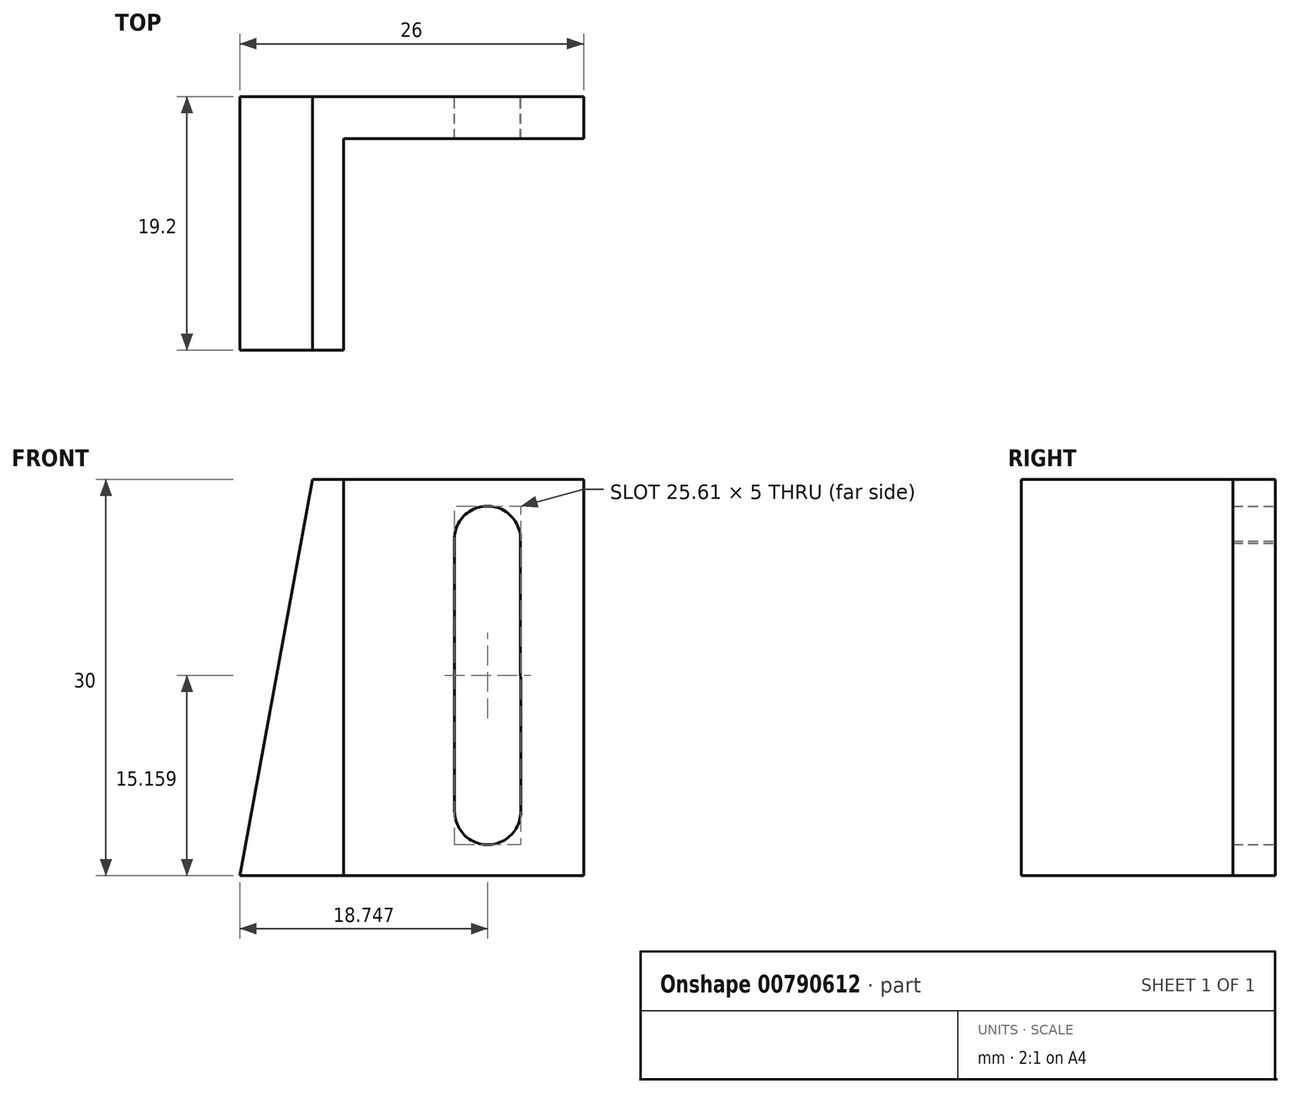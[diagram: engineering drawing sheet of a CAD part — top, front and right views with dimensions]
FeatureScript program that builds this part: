
annotation { "Feature Type Name" : "Feature", "Feature Type Description" : "" }
export const myFeature = defineFeature(function(context is Context, id is Id, definition is map)
    precondition{}
    {
        {
            var Q0;
            Q0=qCreatedBy(makeId("Front.planeOp"),FACE);
            var sketch = newSketch(context, id + "F0", { "sketchPlane" : qUnion([Q0])});
            skLineSegment(sketch, "E0", {"start": v(0, 30) * mm, "end": v(0, 0) * mm});
            skLineSegment(sketch, "E1", {"start": v(-18, 0) * mm, "end": v(-26, 0) * mm});
            skLineSegment(sketch, "E2", {"start": v(-26, 0) * mm, "end": v(-20.5, 30) * mm});
            skLineSegment(sketch, "E3", {"start": v(-20.5, 30) * mm, "end": v(0, 30) * mm});
            skLineSegment(sketch, "E4", {"start": v(-18, 0) * mm, "end": v(0, 0) * mm});
            skLineSegment(sketch, "E5", {"start": v(-18, 0) * mm, "end": v(-18, 30) * mm});
            skArc(sketch, "E6", {"start": v(-4.78, 25.31) * mm, "mid": v(-7.35, 27.96) * mm, "end": v(-9.75, 25.16) * mm});
            skArc(sketch, "E7", {"start": v(-9.75, 4.86) * mm, "mid": v(-7.25, 2.36) * mm, "end": v(-4.75, 4.86) * mm});
            skLineSegment(sketch, "E8", {"start": v(-9.75, 25.16) * mm, "end": v(-9.75, 4.86) * mm});
            skLineSegment(sketch, "E9", {"start": v(-4.78, 25.31) * mm, "end": v(-4.75, 4.86) * mm});
            skSolve(sketch);
        }
        {
            var Q0;
            {var subQ2=sQuery(id+"F0.wireOp",EDGE,"E0");Q0=makeQuery(id+"F0.imprint","IMPRINT",FACE,{"disambiguationData":[TD([[makeQuery(id+"F0.imprint","IMPRINT",EDGE,{"derivedFrom":subQ2}),-1.0]])]});}
            var Q1;
            Q1=makeQuery(id+"F0.imprint","IMPRINT",FACE,{"disambiguationData":[TD([[makeQuery(id+"F0.imprint","IMPRINT",EDGE,{"derivedFrom":sQuery(id+"F0.wireOp",EDGE,"E1")}),-1.0]])]});
            extrude(context, id + "F1", {"entities" : qUnion([Q0, Q1]), "depth" : 3.2 * mm, "offsetDistance" : 25 * mm});
        }
        {
            var Q0;
            Q0=makeQuery(id+"F1.opExtrude","CAP_FACE",FACE,{"disambiguationData":[OSD([sQuery(id+"F0.wireOp",EDGE,"E0"),sQuery(id+"F0.wireOp",EDGE,"E1"),sQuery(id+"F0.wireOp",EDGE,"E2"),sQuery(id+"F0.wireOp",EDGE,"E3"),sQuery(id+"F0.wireOp",EDGE,"E4"),sQuery(id+"F0.wireOp",EDGE,"E6"),sQuery(id+"F0.wireOp",EDGE,"E7"),sQuery(id+"F0.wireOp",EDGE,"E8"),sQuery(id+"F0.wireOp",EDGE,"E9")])],"isStart":false});
            var sketch = newSketch(context, id + "F2", { "sketchPlane" : qUnion([Q0])});
            skLineSegment(sketch, "E10", {"start": v(-18.14, 30) * mm, "end": v(-18.14, 0) * mm});
            skLineSegment(sketch, "E11", {"start": v(-18.14, 30) * mm, "end": v(-20.5, 30) * mm});
            skLineSegment(sketch, "E12", {"start": v(-20.5, 30) * mm, "end": v(-26, 0) * mm});
            skLineSegment(sketch, "E13", {"start": v(-26, 0) * mm, "end": v(-18.14, 0) * mm});
            skSolve(sketch);
        }
        {
            var Q0;
            Q0=makeQuery(id+"F2.imprint","IMPRINT",FACE,{"disambiguationData":[TD([[makeQuery(id+"F2.imprint","IMPRINT",EDGE,{"derivedFrom":sQuery(id+"F2.wireOp",EDGE,"E10")}),-1.0]])]});
            extrude(context, id + "F3", {"entities" : qUnion([Q0]), "operationType" : NewBodyOperationType.ADD, "depth" : 16 * mm, "offsetDistance" : 25 * mm});
        }
    });
